# Revit family: Control_Unit-Lutron-MQSE-2A1(3A1)(4A1)-D
name_source: partatom
category: Lighting Devices
revit_build: Autodesk Revit 2017 (Build: 20160225_1515(x64)
units: mm (PartAtom-declared; Revit-internal decimal feet)

## family parameters
Cut with Voids When Loaded = No
Host = Face
Maintain Annotation Orientation = Yes
OmniClass Number = 23.85.80.11
OmniClass Title = Building Controls
Part Type = Normal
Room Calculation Point = No
Round Connector Dimension = Use Radius
Shared = No

## types (3) — shared parameters
Assembly Code = D5020200
Default Elevation = 48 "
Description = The Phase Adaptive Power Module family is a group of modular products for the control of lighting loads. This product is compatible with Lutron myRoom guestroom systems only.
Finish = Plastic - Lutron - White - Matte
Instruction Sheet Link = http://www.lutron.com
Load Classification = Other
Manufacturer = Lutron Electronics Co., Inc
Manufacturer Fax Number = 610-282-1243
Maximum Operating Temperature = 104 °F
Minimum Operating Temperature = 32 °F
Number of Poles = 1
Overall Depth = 3.53 "
Overall Height = 2.38 "
Overall Width = 6.37 "
Performance URL = http://www.lutron.com
Product Documentation Link = http://www.lutron.com
Product Name = DIN Power Module - Phase Adaptive
Product Page URL = http://www.lutron.com
Series = myRoom
URL = http://www.lutron.com
Version = 2017 - v1.0a
Video Link = https://www.youtube.com
Voltage = 120 V
Warranty URL = http://www.lutron.com
zero-valued in all types: Cost

## per-type parameters (varying)
| type | Apparent Power | Current | Operating Voltage |
| MQSE-4A1-D | 480 VA | 4 A | 100–120 V~, 220–240 V~ 50/60 Hz |
| MQSE-3A1-D | 360 VA | 3 A | 120–240 V~ 50/60 Hz |
| MQSE-2A1-D | 240 VA | 2 A | 120–240 V~ 50/60 Hz |

note: column(s) folded — value = type name in every type: Model

## geometry (parser evidence)
native form markers: Sweep x2
no freeform markers — native parametric forms only
